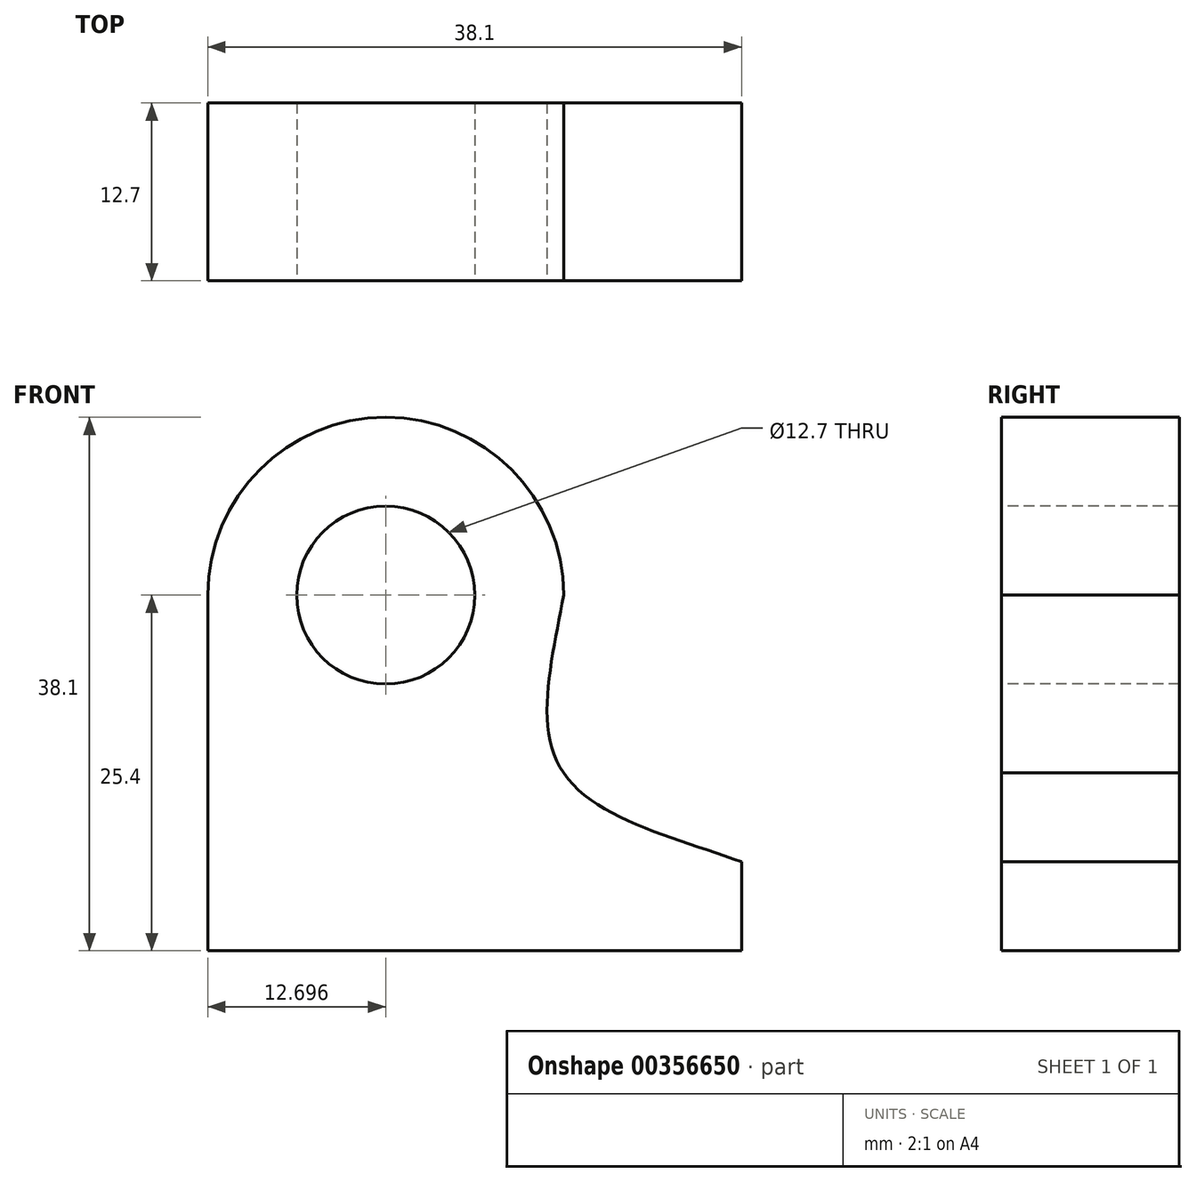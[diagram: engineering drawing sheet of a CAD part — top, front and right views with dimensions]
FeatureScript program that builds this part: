
annotation { "Feature Type Name" : "Feature", "Feature Type Description" : "" }
export const myFeature = defineFeature(function(context is Context, id is Id, definition is map)
    precondition{}
    {
        {
            var Q0;
            Q0=qCreatedBy(makeId("Front.planeOp"),FACE);
            var sketch = newSketch(context, id + "F0", { "sketchPlane" : qUnion([Q0])});
            skLineSegment(sketch, "E0", {"start": v(-45.84, 0) * mm, "end": v(17.66, 0) * mm});
            skLineSegment(sketch, "E1", {"start": v(17.66, 0) * mm, "end": v(17.66, 6.35) * mm});
            skLineSegment(sketch, "E2", {"start": v(17.66, 6.35) * mm, "end": v(-45.84, 6.35) * mm});
            skLineSegment(sketch, "E3", {"start": v(-45.84, 6.35) * mm, "end": v(-45.84, 0) * mm});
            skSolve(sketch);
        }
        {
            var Q0;
            Q0 = qSketchRegion(id + "F0", true);
            extrude(context, id + "F1", {"entities" : qUnion([Q0]), "depth" : 38.1 * mm});
        }
        {
            var Q0;
            Q0=makeQuery(id+"F1.opExtrude","CAP_FACE",FACE,{"disambiguationData":[OSD([sQuery(id+"F0.wireOp",EDGE,"E0"),sQuery(id+"F0.wireOp",EDGE,"E1"),sQuery(id+"F0.wireOp",EDGE,"E2"),sQuery(id+"F0.wireOp",EDGE,"E3")])],"isStart":true});
            var sketch = newSketch(context, id + "F2", { "sketchPlane" : qUnion([Q0])});
            skLineSegment(sketch, "E4", {"start": v(45.84, 6.35) * mm, "end": v(45.84, 44.45) * mm});
            skLineSegment(sketch, "E5", {"start": v(45.84, 44.45) * mm, "end": v(20.44, 44.45) * mm});
            skLineSegment(sketch, "E6", {"start": v(20.44, 44.45) * mm, "end": v(20.44, 6.35) * mm});
            skLineSegment(sketch, "E7", {"start": v(20.44, 6.35) * mm, "end": v(45.84, 6.35) * mm});
            skSolve(sketch);
        }
        {
            var Q0;
            Q0=makeQuery(id+"F2.imprint","IMPRINT",FACE,{"disambiguationData":[TD([[makeQuery(id+"F2.imprint","IMPRINT",EDGE,{"derivedFrom":sQuery(id+"F2.wireOp",EDGE,"E4")}),1.0]])]});
            extrude(context, id + "F3", {"entities" : qUnion([Q0]), "operationType" : NewBodyOperationType.ADD, "oppositeDirection" : true, "depth" : 12.7 * mm});
        }
        {
            var Q0;
            Q0=makeQuery(id+"F3.opExtrude","CAP_FACE",FACE,{"disambiguationData":[OSD([sQuery(id+"F2.wireOp",EDGE,"E4"),sQuery(id+"F2.wireOp",EDGE,"E5"),sQuery(id+"F2.wireOp",EDGE,"E6"),sQuery(id+"F2.wireOp",EDGE,"E7")])],"isStart":false});
            var sketch = newSketch(context, id + "F4", { "sketchPlane" : qUnion([Q0])});
            skArc(sketch, "E8", {"start": v(-20.44, 25.4) * mm, "mid": v(-33.14, 38.1) * mm, "end": v(-45.84, 25.4) * mm});
            skSolve(sketch);
        }
        {
            var Q0;
            {var subQ0=sQuery(id+"F4.wireOp",EDGE,"E8");Q0=makeQuery(id+"F4.imprint","IMPRINT",FACE,{"disambiguationData":[TD([[makeQuery(id+"F4.imprint","IMPRINT",EDGE,{"derivedFrom":subQ0}),-1.0]])]});}
            extrude(context, id + "F5", {"entities" : qUnion([Q0]), "operationType" : NewBodyOperationType.REMOVE, "oppositeDirection" : true, "depth" : 25.4 * mm});
        }
        {
            var Q0;
            Q0=makeQuery(id+"F3.opExtrude","CAP_FACE",FACE,{"disambiguationData":[OSD([sQuery(id+"F2.wireOp",EDGE,"E4"),sQuery(id+"F2.wireOp",EDGE,"E5"),sQuery(id+"F2.wireOp",EDGE,"E6"),sQuery(id+"F2.wireOp",EDGE,"E7")])],"isStart":false});
            var sketch = newSketch(context, id + "F6", { "sketchPlane" : qUnion([Q0])});
            skCircle(sketch, "E9", {"center": v(-33.14, 25.4) * mm, "radius": 6.35 * mm});
            skSolve(sketch);
        }
        {
            var Q0;
            Q0 = qSketchRegion(id + "F6", true);
            extrude(context, id + "F7", {"entities" : qUnion([Q0]), "operationType" : NewBodyOperationType.REMOVE, "oppositeDirection" : true, "depth" : 25.4 * mm});
        }
        {
            var Q0;
            Q0=makeQuery(id+"F3.opExtrude","CAP_FACE",FACE,{"disambiguationData":[OSD([sQuery(id+"F2.wireOp",EDGE,"E4"),sQuery(id+"F2.wireOp",EDGE,"E5"),sQuery(id+"F2.wireOp",EDGE,"E6"),sQuery(id+"F2.wireOp",EDGE,"E7")])],"isStart":false});
            var sketch = newSketch(context, id + "F8", { "sketchPlane" : qUnion([Q0])});
            skLineSegment(sketch, "E10", {"start": v(-20.44, 6.35) * mm, "end": v(-20.44, 12.7) * mm});
            skFitSpline(sketch, "E11", {"points": [v(-20.44, 25.4) * mm, v(-20.44, 12.7) * mm, v(-7.74, 6.35) * mm], "startDerivative": vector(-4.74, -27.32) * mm, "endDerivative": vector(22.58, -10.56) * mm});
            skLineSegment(sketch, "E12", {"start": v(-20.44, 6.35) * mm, "end": v(-7.74, 6.35) * mm});
            skSolve(sketch);
        }
        {
            var Q0;
            {var subQ0=sQuery(id+"F8.wireOp",EDGE,"E11");var subQ1=makeQuery(id+"F3.opExtrude","CAP_EDGE",EDGE,{"disambiguationData":[OSD([sQuery(id+"F2.wireOp",EDGE,"E6")])],"isStart":false});var subQ2=makeQuery(id+"F8.imprint","INTERSECT",VERTEX,{"derivedFrom":[makeQuery(id+"F5.boolean.opBoolean","COPY",EDGE,{"derivedFrom":makeQuery(id+"F5.opExtrude","CAP_EDGE",EDGE,{"disambiguationData":[OSD([sQuery(id+"F4.wireOp",EDGE,"E8")])],"isStart":true})}),subQ1,subQ0]});Q0=makeQuery(id+"F8.imprint","IMPRINT",FACE,{"disambiguationData":[TD([[makeQuery(id+"F8.imprint","IMPRINT",EDGE,{"disambiguationData":[TD([[subQ2,-1.0]])],"derivedFrom":subQ0}),1.0]])]});}
            extrude(context, id + "F9", {"entities" : qUnion([Q0]), "operationType" : NewBodyOperationType.REMOVE, "oppositeDirection" : true, "depth" : 25.4 * mm});
        }
        {
            var Q0;
            Q0=makeQuery(id+"F3.opExtrude","CAP_FACE",FACE,{"disambiguationData":[OSD([sQuery(id+"F2.wireOp",EDGE,"E4"),sQuery(id+"F2.wireOp",EDGE,"E5"),sQuery(id+"F2.wireOp",EDGE,"E6"),sQuery(id+"F2.wireOp",EDGE,"E7")])],"isStart":false});
            var sketch = newSketch(context, id + "F10", { "sketchPlane" : qUnion([Q0])});
            skFitSpline(sketch, "E13", {"points": [v(-20.44, 25.4) * mm, v(-20.44, 12.7) * mm, v(-7.74, 6.35) * mm], "startDerivative": vector(-5.31, -28.25) * mm, "endDerivative": vector(26.23, -9.78) * mm});
            skLineSegment(sketch, "E14", {"start": v(-7.74, 6.35) * mm, "end": v(-20.44, 6.35) * mm});
            skLineSegment(sketch, "E15", {"start": v(-20.44, 6.35) * mm, "end": v(-20.44, 12.7) * mm});
            skSolve(sketch);
        }
        {
            var Q0;
            Q0 = qSketchRegion(id + "F10", true);
            extrude(context, id + "F11", {"entities" : qUnion([Q0]), "operationType" : NewBodyOperationType.ADD, "oppositeDirection" : true, "depth" : 12.7 * mm});
        }
        {
            var Q0;
            Q0=makeQuery(id+"F1.opExtrude","SWEPT_FACE",FACE,{"disambiguationData":[OSD([sQuery(id+"F0.wireOp",EDGE,"E2")])]});
            var sketch = newSketch(context, id + "F12", { "sketchPlane" : qUnion([Q0])});
            skLineSegment(sketch, "E16", {"start": v(17.66, 0) * mm, "end": v(17.66, -19.05) * mm});
            skLineSegment(sketch, "E17", {"start": v(17.66, -19.05) * mm, "end": v(-45.84, -19.05) * mm});
            skPoint(sketch, "E17.endSnap0", {"position": v(-45.84, -25.4) * mm});
            skCircle(sketch, "E18", {"center": v(8.13, -9.26) * mm, "radius": 3.44 * mm});
            skCircle(sketch, "E19", {"center": v(8.13, -28.58) * mm, "radius": 3.18 * mm});
            skCircle(sketch, "E20", {"center": v(-36.32, -28.58) * mm, "radius": 3.17 * mm});
            skCircle(sketch, "E21", {"center": v(8.13, -28.58) * mm, "radius": 9.87 * mm});
            skCircle(sketch, "E22", {"center": v(-36.32, -28.58) * mm, "radius": 9.56 * mm});
            skSolve(sketch);
        }
        {
            var Q0;
            Q0=makeQuery(id+"F12.imprint","IMPRINT",FACE,{"disambiguationData":[TD([[makeQuery(id+"F12.imprint","IMPRINT",EDGE,{"derivedFrom":sQuery(id+"F12.wireOp",EDGE,"E18")}),1.0]])]});
            extrude(context, id + "F13", {"entities" : qUnion([Q0]), "operationType" : NewBodyOperationType.REMOVE, "oppositeDirection" : true, "depth" : 25.4 * mm});
        }
        {
            var Q0;
            Q0=makeQuery(id+"F1.opExtrude","SWEPT_FACE",FACE,{"disambiguationData":[OSD([sQuery(id+"F0.wireOp",EDGE,"E2")])]});
            extrude(context, id + "F14", {"entities" : qUnion([Q0]), "operationType" : NewBodyOperationType.REMOVE, "oppositeDirection" : true, "depth" : 25.4 * mm});
        }
    });
